# Revit family: Caldaria 55.1 Condensing+_en
name_source: partatom
category: Modelli generici
revit_build: Autodesk Revit 2017 (Build: 20160225_1515(x64)
units: mm (PartAtom-declared; Revit-internal decimal feet)

## family parameters
Basato su piano di lavoro = No
Condiviso = No
Punto di calcolo locali = No
Può ospitare armatura = No
Quota connettore circolare = Usa diametro
Sempre verticale = Sì
Taglio con vuoti quando caricato = No
Tipo di parte = Normale

## types (1)
- Caldaia 55.1 Condensing+_EN
    A01. Seasonal space heating energy efficiency class (ErP) = A
    A02. Heat input - nominal (1013 mbar - 15 °C) = 50 kW
    A03. Heat input - minimum = 5 kW
    A04. Operating point 80/60 - Nominal heat input - effective power = 49 kW
    A05. Operating point 80/60 - Nominal heat input - Efficiency = 98.40%
    A06. Operating point 50/30 - Nominal heat input - Efficiency = 106.80%
    A07. Operating point Tr=30 °C - Heat input 30% - Efficiency = 108.80%
    A08. Operating point Tr=47 °C - Heat input 30% - Efficiency = 102.80%
    A09. Heat loss - to jacket in operation = 0.10%
    A10. Heat loss - to flue in operation = 2.10%
    A11. Heat loss - with burner off = 0.05%
    A12. Hot water delivery temperature - maximum = 80 °C
    A13. Ambient air temperature (dry bulb) - maximum = 60 °C
    A14. Ambient air temperature (dry bulb) - minimum = -25 °C
    B01. Power supply - voltage = 230 V
    B02. Power supply - type = single-phase
    B03. Power supply - frequency = 50 Hz
    B04. Electrical power absorption - nominal = 0 kW
    B05. Degree of protection - IP = X5D
    BIMobject category = Boilers
    BIMobject category code = hvac-boilers
    BIMobject main category = HVAC
    BIMobject main category code = hvac
    Brand url = https://www.robur.com
    C01. Gas Comsumption - G20 natural gas (nominal) = 5.3 m³/h
    C02. Gas consumption - G25 (nominal) = 6.2 m³/h
    C03. Gas consumption - G25.3 (nominal) = 6.0 m³/h
    C04. Gas consumption - G30 (nominal) [kg/h] = 3.94
    C05. Gas consumption - G31 (nominal) [kg/h] = 3.88
    C06. Water fitting - type = M
    C07. Water fitting - thread = 1 1/2"
    C08. Gas connection - type = M
    C09. Gas connection - Thread = 1"
    C10. Flue gas exhaust - diameter = 80 mm
    C11. Flue gas exhaust - residual head = 100.0 Pa
    C12. NOx emission class = 6
    C13. Circulating pump data - Residual pressure head at numinal flow rate - boiler only [m.w.c.] = 5.1
    C14. Circulating pump data - nominal flow at the maximum available head [l/h] = 2150
    C15. Type of installation = B23P, B33
    C16. Maximum equivalent lenght of exhaust duct = 14.0 m
    C17. Maximum water pressure in operation = 3.0 barra
    C18. Maximum flow flue condensate [l/h] = 5
    C19. Water content inside the apparatus = 9.00 L
    C20. Expansion tank volume = 10.00 L
    C21. Dimensions - Width = 480 mm
    C22. Dimensions - Depth = 600 mm
    C23. Dimensions - Height = 869 mm
    C24. Weight - in operation = 54.00 kg
    Design country = Italy
    Edition number = 1
    IFC Classification = Boiler
    Installation instructions = https://www.robur.com
    Manufacturer country = Italy
    Manufacturer name = Robur
    Masterformat 2014 Code = 23 52 16
    Masterformat 2014 Description = Condensing Boilers
    Material main = Stainless steel
    NBS Reference Code = 60-08-36
    NBS Reference Description = Condensing Boilers
    Nominal height = 869 mm
    Nominal width = 480 mm
    OmniClass Code = 23-33 11 13
    OmniClass Description = Condensing Boilers
    Product Guid = d5bceecd-734e-4a58-b804-701b90ea27c3
    Product SKU = Caldaria_55-1_Condensing_Plus_export
    Product certification = https://www.robur.com
    Product data url = https://bimobject.com
    Product family = Boilers
    Product group = Boiler
    Product url = https://www.robur.com
    QR code = http://bimobject.com
    UNSPSC Code = 401020
    Uniclass 1.4 Code = L75211
    Uniclass 1.4 Description = Gas fired boilers
    Uniclass 2.0 Code = PR-60-08-36
    Uniclass 2.0 Description = Condensing Boilers
    Uniclass 2015 Code = Pr_60_60_08_34
    Uniclass 2015 Name = Gas fired condensing boilers
    Uniformat II Code = D3020
    Uniformat II Description = Heat Generating Systems
    Weight Net (Kg) = 54
    Youtube clip = https://youtu.be
